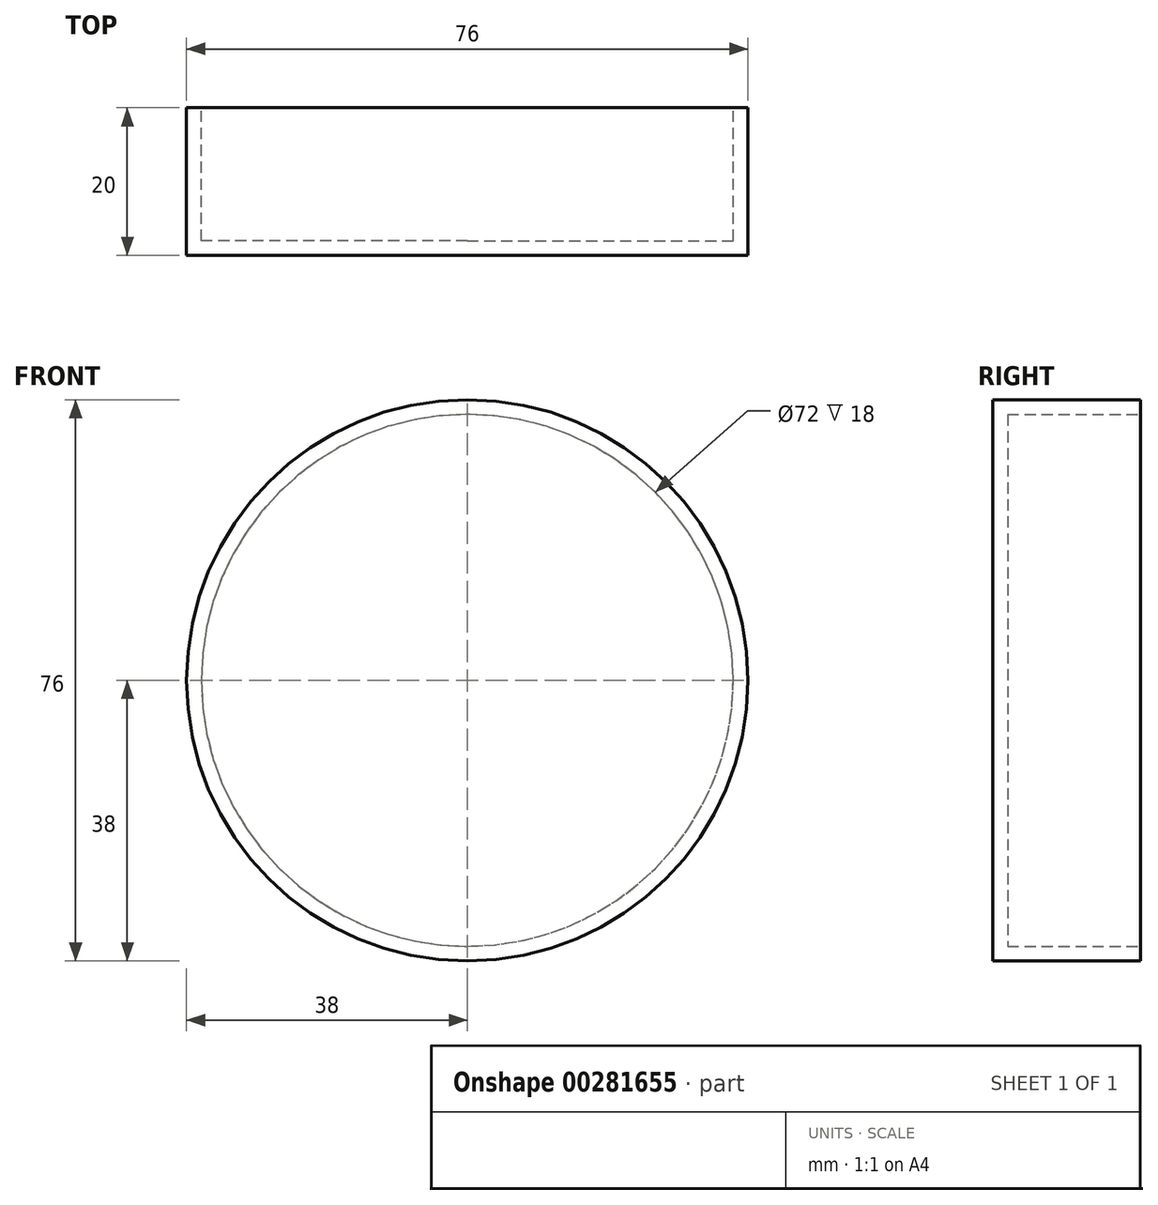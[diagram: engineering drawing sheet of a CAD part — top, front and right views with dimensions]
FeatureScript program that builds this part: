
annotation { "Feature Type Name" : "Feature", "Feature Type Description" : "" }
export const myFeature = defineFeature(function(context is Context, id is Id, definition is map)
    precondition{}
    {
        {
            var Q0;
            Q0=qCreatedBy(makeId("Top.planeOp"),FACE);
            var sketch = newSketch(context, id + "F0", { "sketchPlane" : qUnion([Q0])});
            skLineSegment(sketch, "E0", {"start": v(0, 0) * mm, "end": v(-38, 0) * mm});
            skLineSegment(sketch, "E1", {"start": v(-38, 0) * mm, "end": v(-38, -20) * mm});
            skLineSegment(sketch, "E2", {"start": v(-38, -20) * mm, "end": v(0, -20) * mm});
            skLineSegment(sketch, "E3", {"start": v(0, 0) * mm, "end": v(0, -20) * mm});
            skSolve(sketch);
        }
        {
            var Q0;
            Q0 = qSketchRegion(id + "F0", true);
            var Q1;
            Q1=sQuery(id+"F0.wireOp",EDGE,"E3");
            revolve(context, id + "F1", {"entities" : qUnion([Q0]), "axis" : qUnion([Q1]), "revolveType" : RevolveType.FULL});
        }
        {
            var Q0;
            Q0=makeQuery(id+"F1.opRevolve","SWEPT_FACE",FACE,{"disambiguationData":[OSD([sQuery(id+"F0.wireOp",EDGE,"E0")])]});
            shell(context, id + "F2", {"entities" : qUnion([Q0]), "thickness" : 2 * mm});
        }
    });
